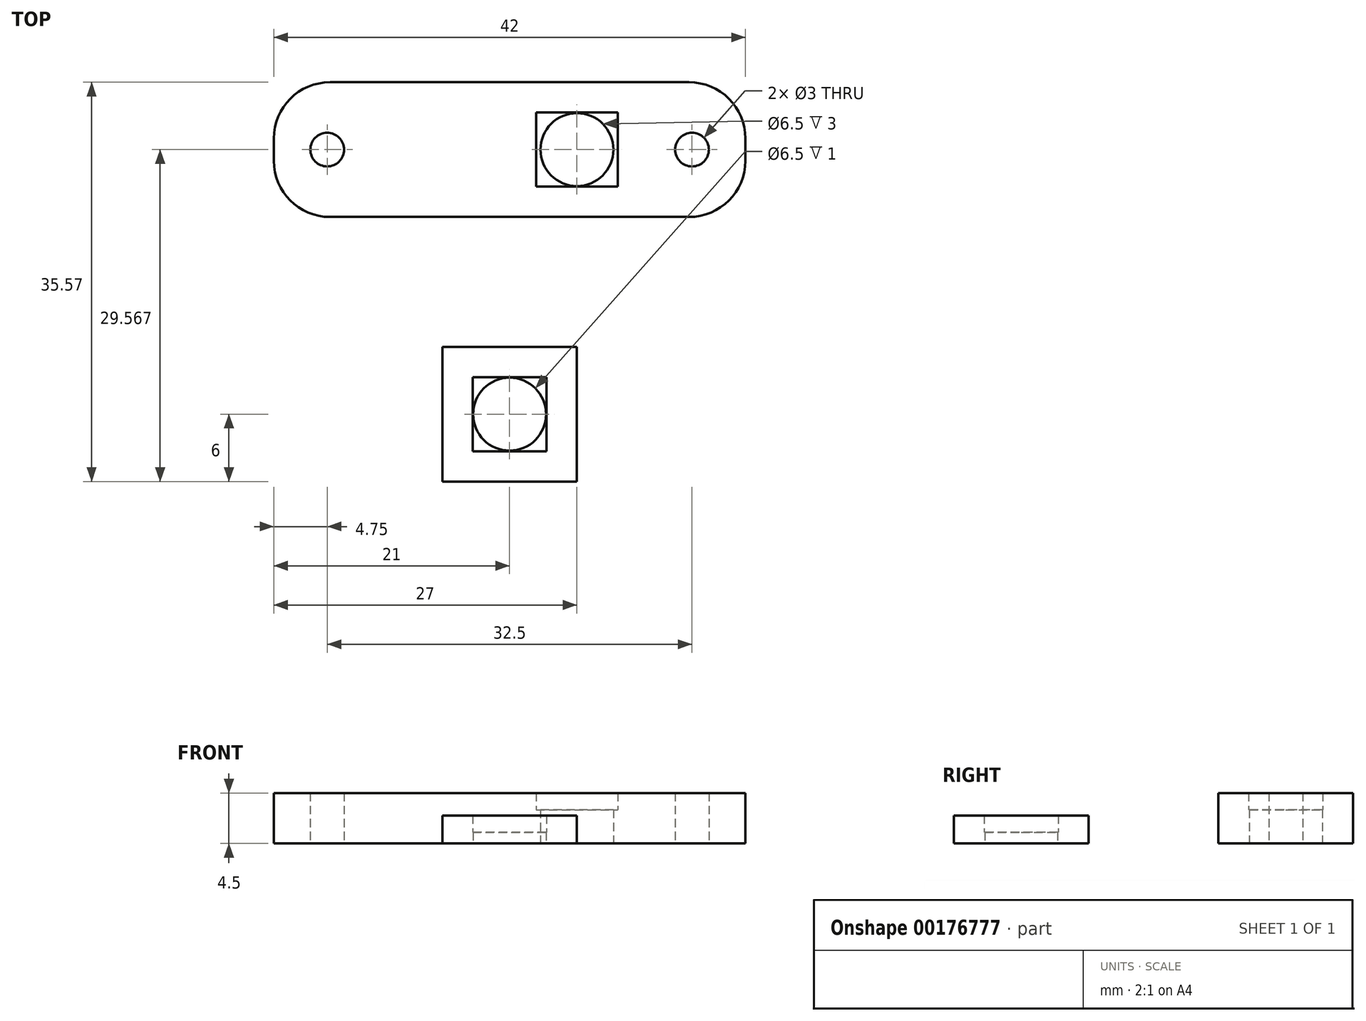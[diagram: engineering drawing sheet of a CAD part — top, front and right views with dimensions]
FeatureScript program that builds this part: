
annotation { "Feature Type Name" : "Feature", "Feature Type Description" : "" }
export const myFeature = defineFeature(function(context is Context, id is Id, definition is map)
    precondition{}
    {
        {
            assignVariable(context, id + "F0", {"name" : "frameThickness", "anyValue" : 2});
        }
        {
            assignVariable(context, id + "F1", {"name" : "threadGap", "anyValue" : 3});
        }
        {
            assignVariable(context, id + "F2", {"name" : "mountSquareThickness", "anyValue" : 1.5});
        }
        {
            var Q0;
            Q0=qCreatedBy(makeId("Top.planeOp"),FACE);
            var sketch = newSketch(context, id + "F3", { "sketchPlane" : qUnion([Q0])});
            skLineSegment(sketch, "E0.bottom", {"start": v(-6, 6) * mm, "end": v(6, 6) * mm});
            skLineSegment(sketch, "E0.top", {"start": v(-6, -6) * mm, "end": v(6, -6) * mm});
            skLineSegment(sketch, "E0.left", {"start": v(-6, 6) * mm, "end": v(-6, -6) * mm});
            skLineSegment(sketch, "E0.right", {"start": v(6, 6) * mm, "end": v(6, -6) * mm});
            skPoint(sketch, "E0.middle", {"position": v(0, 0) * mm});
            skCircle(sketch, "E1", {"center": v(0, 0) * mm, "radius": 3.25 * mm});
            skSolve(sketch);
        }
        {
            var Q0;
            Q0=qSketchRegion(id+"F3",true);
            extrude(context, id + "F4", {"entities" : qUnion([Q0]), "depth" : (getVariable(context, 'threadGap') - getVariable(context, 'frameThickness')) * mm});
        }
        {
            var Q0;
            Q0=makeQuery(id+"F4.opExtrude","CAP_FACE",FACE,{"disambiguationData":[OSD([sQuery(id+"F3.wireOp",EDGE,"E0.bottom"),sQuery(id+"F3.wireOp",EDGE,"E0.top"),sQuery(id+"F3.wireOp",EDGE,"E0.left"),sQuery(id+"F3.wireOp",EDGE,"E0.right"),sQuery(id+"F3.wireOp",EDGE,"E1")])],"isStart":false});
            var sketch = newSketch(context, id + "F5", { "sketchPlane" : qUnion([Q0])});
            skLineSegment(sketch, "E2.bottom", {"start": v(-3.3, 3.3) * mm, "end": v(3.3, 3.3) * mm});
            skLineSegment(sketch, "E2.top", {"start": v(-3.3, -3.3) * mm, "end": v(3.3, -3.3) * mm});
            skLineSegment(sketch, "E2.left", {"start": v(-3.3, 3.3) * mm, "end": v(-3.3, -3.3) * mm});
            skLineSegment(sketch, "E2.right", {"start": v(3.3, 3.3) * mm, "end": v(3.3, -3.3) * mm});
            skPoint(sketch, "E2.middle", {"position": v(0, 0) * mm});
            skLineSegment(sketch, "E3.bottom", {"start": v(-6, 6) * mm, "end": v(6, 6) * mm});
            skLineSegment(sketch, "E3.top", {"start": v(-6, -6) * mm, "end": v(6, -6) * mm});
            skLineSegment(sketch, "E3.left", {"start": v(-6, 6) * mm, "end": v(-6, -6) * mm});
            skLineSegment(sketch, "E3.right", {"start": v(6, 6) * mm, "end": v(6, -6) * mm});
            skSolve(sketch);
        }
        {
            var Q0;
            Q0=qSketchRegion(id+"F5",true);
            extrude(context, id + "F6", {"entities" : qUnion([Q0]), "operationType" : NewBodyOperationType.ADD, "depth" : (getVariable(context, 'mountSquareThickness')) * mm});
        }
        {
            var Q0;
            Q0=qCreatedBy(makeId("Top.planeOp"),FACE);
            var sketch = newSketch(context, id + "F7", { "sketchPlane" : qUnion([Q0])});
            skLineSegment(sketch, "E4.bottom", {"start": v(-21, 29.57) * mm, "end": v(21, 29.57) * mm});
            skLineSegment(sketch, "E4.top", {"start": v(-21, 17.57) * mm, "end": v(21, 17.57) * mm});
            skLineSegment(sketch, "E4.left", {"start": v(-21, 29.57) * mm, "end": v(-21, 17.57) * mm});
            skLineSegment(sketch, "E4.right", {"start": v(21, 29.57) * mm, "end": v(21, 17.57) * mm});
            skPoint(sketch, "E4.middle", {"position": v(0, 23.57) * mm});
            skCircle(sketch, "E5", {"center": v(-16.25, 23.57) * mm, "radius": 1.5 * mm});
            skCircle(sketch, "E6", {"center": v(16.25, 23.57) * mm, "radius": 1.5 * mm});
            skCircle(sketch, "E7", {"center": v(6, 23.57) * mm, "radius": 3.25 * mm});
            skLineSegment(sketch, "E8.bottom", {"start": v(2.35, 26.87) * mm, "end": v(9.65, 26.87) * mm});
            skLineSegment(sketch, "E8.top", {"start": v(2.35, 20.27) * mm, "end": v(9.65, 20.27) * mm});
            skLineSegment(sketch, "E8.left", {"start": v(2.35, 26.87) * mm, "end": v(2.35, 20.27) * mm});
            skLineSegment(sketch, "E8.right", {"start": v(9.65, 26.87) * mm, "end": v(9.65, 20.27) * mm});
            skSolve(sketch);
        }
        {
            var Q0;
            Q0 = qSketchRegion(id + "F7", true);
            extrude(context, id + "F8", {"entities" : qUnion([Q0]), "depth" : (getVariable(context, 'threadGap') + getVariable(context, 'mountSquareThickness')) * mm});
        }
        {
            var Q0;
            Q0=makeQuery(id+"F7.imprint","IMPRINT",FACE,{"disambiguationData":[TD([[makeQuery(id+"F7.imprint","IMPRINT",EDGE,{"derivedFrom":sQuery(id+"F7.wireOp",EDGE,"E7")}),-1.0]])]});
            extrude(context, id + "F9", {"entities" : qUnion([Q0]), "operationType" : NewBodyOperationType.ADD, "depth" : (getVariable(context, 'threadGap')) * mm});
        }
        {
            var Q0;
            Q0=makeQuery(id+"F8.opExtrude","SWEPT_EDGE",EDGE,{"disambiguationData":[OSD([sQuery(id+"F7.wireOp",EDGE,"E4.top"),sQuery(id+"F7.wireOp",EDGE,"E4.right")])]});
            var Q1;
            Q1=makeQuery(id+"F8.opExtrude","SWEPT_EDGE",EDGE,{"disambiguationData":[OSD([sQuery(id+"F7.wireOp",EDGE,"E4.top"),sQuery(id+"F7.wireOp",EDGE,"E4.left")])]});
            var Q2;
            Q2=makeQuery(id+"F8.opExtrude","SWEPT_EDGE",EDGE,{"disambiguationData":[OSD([sQuery(id+"F7.wireOp",EDGE,"E4.bottom"),sQuery(id+"F7.wireOp",EDGE,"E4.right")])]});
            var Q3;
            Q3=makeQuery(id+"F8.opExtrude","SWEPT_EDGE",EDGE,{"disambiguationData":[OSD([sQuery(id+"F7.wireOp",EDGE,"E4.bottom"),sQuery(id+"F7.wireOp",EDGE,"E4.left")])]});
            fillet(context, id + "F10", {"entities" : qUnion([Q0, Q1, Q2, Q3]), "radius" : 5 * mm, "tangentPropagation" : true, "allowEdgeOverflow" : false});
        }
    });
